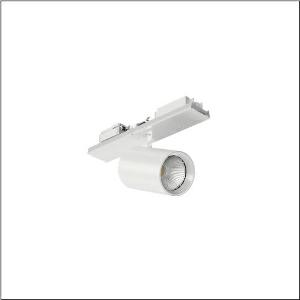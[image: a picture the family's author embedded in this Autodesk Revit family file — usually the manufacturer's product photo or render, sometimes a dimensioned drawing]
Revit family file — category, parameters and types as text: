
# Revit family: licross_r__spot_31_51sl14da43b_e1eb
name_source: partatom
category: Lighting Fixtures
units: mm (PartAtom-declared; Revit-internal decimal feet)

## family parameters
Cut with Voids When Loaded = No
Host = Face
Light Source = No
Part Type = Normal
Room Calculation Point = No
Round Connector Dimension = Use Diameter
Shared = No

## types (1)
- --- (1 x LED, 3720 lm, 28.5 W, 4000K)
    Apparent Load = 29 VA
    CIE Flux Codes = 93 97 100 100 100
    Color Rendering = 90
    Color Temperature = 4000K
    Default Elevation = 1800 mm
    Description = Licross® Spot 31, directional spotlight, light control with lens, of plastic, LED rated luminous flux: 3.720lm, light colour: 940, with plug, 5-pole, mains connection: 220..240V, AC, 50/60Hz, of aluminium, traffic white (RAL 9016), length: 300mm, diameter: 90mm, protection rating (complete): IP20, insulation class (complete): insulation class I (protective earthing), certification: CE, packaging unit: 1 piece
    Height = 175 mm
    Lamp = 1 x LED
    Lamp Light Flux = 3720 lm
    Lamp Power = 28.5 W
    Lamp count = 1
    Length = 90 mm
    Luminous efficacy = 131 lm/W
    Manufacturer = Siteco
    ModVariant = No
    Model = 51SL14DA43B
    Mounting Place = Ceiling
    Mounting Type = Pendant
    Number of Poles = 1
    OnlyDefault = Yes
    Power Factor = 1
    Product Name = Licross® Spot 31
    Product group = directional spotlight
    ProductGroupID = 905
    Protection Class = Protection class I
    Protection Degree = IP 20
    RLX_Detail_Level = 1
    RLX_Emergency_Light_Flux = 0 lm
    RLX_Emergency_Type = 0
    RLX_Emergency_Type_DB = No
    RlxData = <blob elided: 14801 chars, md5=6a1cd4ee>
    Socket = socket
    Standby Power = 0 W
    System Light Flux = 3720 lm
    System Power = 29 W
    Type Comments = factory setting: luminous flux: 100 % | (ON | ON | ON) | 700 mA
    Type Image = l_1245720.jpg
    URL = http://relux.com
    VarID = @adj_102147
    Voltage = 0 V
    Weight = 0.00 kg
    Width = 0 mm  [stored 0 ft]

note: [stored X ft] marks values corroborated as IEEE doubles in the binary element streams (Revit-internal decimal feet)

## geometry (parser evidence)
native form markers: Sweep x11
no freeform markers — native parametric forms only
